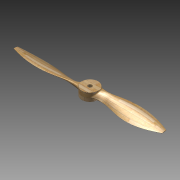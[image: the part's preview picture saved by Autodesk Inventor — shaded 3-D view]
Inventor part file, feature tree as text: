
AUTODESK INVENTOR PART (.ipt)
format: ipt  version: 2011 SP1 (Build 150282100, 282)  size: 843,776 bytes
history: native  units: in
note: dims shown in document units (in); Inventor stores cm internally (conversion verified against a paired STEP export)
features: other x15, sketch x10, plane x8, fillet x4, extrude x2, loft x1, pattern_circular x1, hole x1
ambient origin geometry x8: Origin, YZ Plane, XZ Plane, XY Plane, X Axis, Y Axis, Z Axis, Center Point
feature tree (42):
  sketch  "Sketch1"  dims[d0=36.0in d1=8.0in]
  plane  "Work Plane1"
  plane  "Work Plane3"
  sketch  "Sketch2"  dims[d2=7.0in d5=4.0in d6=0.0in d7=-5.0in d8=0.15in]
  sketch  "Sketch3"  dims[d9=4.0in d10=4.0in d11=8.0in d12=8.0in d13=0.0in d14=90.0deg]
  sketch  "3D Sketch1"
  plane  "Work Plane4"
  plane  "Work Plane5"
  plane  "Work Plane6"
  plane  "Work Plane7"
  plane  "Work Plane8"
  plane  "Work Plane9"
  other  "Work Point1"
  other  "Work Point2"
  other  "Work Point3"
  other  "Work Point4"
  other  "Work Point5"
  other  "Work Point7"
  other  "Work Point8"
  other  "Work Point9"
  other  "Work Point10"
  other  "Work Point11"
  other  "Work Point12"
  other  "Work Point13"
  extrude  "Extrusion2"  Depth=8.0in
  loft  "Loft1"
  fillet  "Fillet1"  [1 undecoded]
  fillet  "Fillet3"  Radius=0.15in
  fillet  "Fillet2"  [1 undecoded]
  pattern_circular  "Circular Pattern1"  Angle=90.0deg  [1 undecoded]
  hole  "Hole1"  [1 undecoded]
  fillet  "Fillet4"  Radius=0.75in
  other  "Srf1"
  other  "Project to Surface2"
  other  "Project to Surface3"
  sketch  "Sketch4"  dims[d15=0.0in d16=90.0deg]
  sketch  "Sketch5"  dims[d17=0.0in d18=90.0deg]
  sketch  "Sketch6"  dims[d19=0.0in d20=90.0deg]
  sketch  "Sketch7"  dims[d21=0.0in d22=90.0deg]
  sketch  "Sketch8"  dims[d23=0.0in d24=90.0deg]
  sketch  "Sketch9"  dims[d25=0.0in d26=90.0deg d27=0.0in d28=90.0deg d29=4.0in d30=0.0in d32=0.75in d33=0.75in d34=0.0625in d35=0.125in d36=0.1292in d37=0.7874in d38=360.0deg d40=1.0in d41=1.0in d42=2.0in d43=0.75in d44=0.375in d45=0.25in d46=0.5635in d47=1.0in d48=0.8108in d49=0.0625in d50=0.75in d51=0.0625in d52=0.125in d53=0.0638in]
  extrude  "ExtrusionSrf1"  Depth=0.75in
note: 4 required parameter values undecoded (feature->parameter linkage not recoverable at this tier; creation-order binding heuristic only, values carry confidence <= 0.55)
